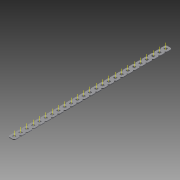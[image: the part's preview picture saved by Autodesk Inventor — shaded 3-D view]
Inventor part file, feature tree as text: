
AUTODESK INVENTOR PART (.ipt)
format: ipt  version: 2015 (Build 190159000, 159)  size: 1,123,328 bytes
history: native  units: in
note: dims shown in document units (in); Inventor stores cm internally (conversion verified against a paired STEP export)
features: other x34, extrude x2, pattern_linear x1, imported_body x1
ambient origin geometry x8: Origin, YZ Plane, XZ Plane, XY Plane, X Axis, Y Axis, Z Axis, Center Point
bodies: Body1 (feature_tree)
feature tree (38):
  other  "Diamond-Pattern"
  other  "Plate"
  extrude  "length cut"  TaperAngle=0.0deg  [1 undecoded]
  extrude  "width cut"  TaperAngle=0.0deg  [1 undecoded]
  other  "constraint axis"
  pattern_linear  "constraint axes"  Spacing1=0.5in  [1 undecoded]
  other  "front plane"
  other  "right plane"
  imported_body  "Base1"
  other  "length profile"
  other  "width profile"
  other  "Work Point1"
  other  "back plane"
  other  "left plane"
  other  "Work Axis170"
  other  "Work Axis171"
  other  "Work Axis172"
  other  "Work Axis173"
  other  "Work Axis174"
  other  "Work Axis175"
  other  "Work Axis176"
  other  "Work Axis177"
  other  "Work Axis178"
  other  "Work Axis229"
  other  "Work Axis230"
  other  "Work Axis231"
  other  "Work Axis232"
  other  "Work Axis233"
  other  "Work Axis234"
  other  "Work Axis235"
  other  "Work Axis236"
  other  "Work Axis237"
  other  "Work Axis238"
  other  "Work Axis239"
  other  "Work Axis240"
  other  "Work Axis241"
  other  "Work Axis242"
  other  "Work Axis243"
note: 3 required parameter values undecoded (feature->parameter linkage not recoverable at this tier; creation-order binding heuristic only, values carry confidence <= 0.55)
